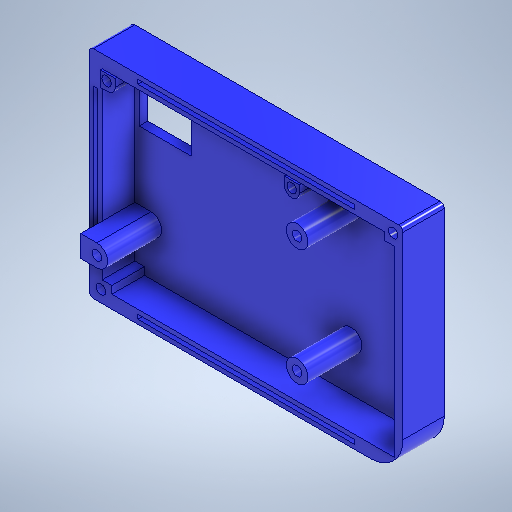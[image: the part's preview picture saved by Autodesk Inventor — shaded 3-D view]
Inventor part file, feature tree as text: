
AUTODESK INVENTOR PART (.ipt)
format: ipt  version: 2025.2 (Build 292293000, 293)  size: 788,992 bytes
history: native  units: mm
features: projected_geometry x22, sketch x19, extrude x13, fillet x2, other x1, hole x1
ambient origin geometry x8: Origin, YZ Plane, XZ Plane, XY Plane, X Axis, Y Axis, Z Axis, Center Point
bodies: Body1 (feature_tree)
feature tree (58):
  other  "Těleso1"
  extrude  "Vysunutí1"  Depth=130.0mm
  extrude  "Vysunutí2"  Depth=100.0mm
  fillet  "Zaoblení1"  Radius=30.0mm
  fillet  "Zaoblení2"  Radius=33.0mm
  extrude  "Vysunutí3"  Depth=4.0mm
  extrude  "Vysunutí4"  Depth=6.0mm
  extrude  "Vysunutí5"  Depth=6.0mm
  extrude  "Vysunutí6"  Depth=6.0mm
  extrude  "Vysunutí7"  Depth=29.0mm TaperAngle=0.0deg
  extrude  "Vysunutí8"  Depth=2.0mm
  extrude  "Vysunutí9"  Depth=2.0mm
  sketch  "Náčrt12"
  sketch  "Náčrt13"
  sketch  "Náčrt15"
  extrude  "Vysunutí10"  Depth=7.0mm
  hole  "Díra1"  [1 undecoded]
  sketch  "Náčrt19"
  extrude  "Vysunutí11"  Depth=85.0mm
  extrude  "Vysunutí13"  Depth=10.0mm
  extrude  "Vysunutí14"  Depth=8.0mm
  sketch  "Náčrt24"
  sketch  "Náčrt1"
  sketch  "Náčrt2"
  projected_geometry  "Promítnutá smyčka1"
  sketch  "Náčrt3"
  projected_geometry  "Promítnutá smyčka2"
  projected_geometry  "Promítnutá smyčka3"
  sketch  "Náčrt4"
  projected_geometry  "Promítnutá smyčka4"
  sketch  "Náčrt6"
  sketch  "Náčrt8"
  projected_geometry  "Promítnutá smyčka5"
  sketch  "Náčrt9"
  projected_geometry  "Promítnutá smyčka6"
  projected_geometry  "Promítnutá smyčka7"
  sketch  "Náčrt10"
  projected_geometry  "Promítnutá smyčka8"
  projected_geometry  "Promítnutá smyčka9"
  sketch  "Náčrt11"
  projected_geometry  "Promítnutá smyčka10"
  projected_geometry  "Promítnutá smyčka11"
  projected_geometry  "Promítnutá smyčka12"
  projected_geometry  "Promítnutá smyčka13"
  projected_geometry  "Promítnutá smyčka14"
  projected_geometry  "Promítnutá smyčka16"
  sketch  "Náčrt16"
  sketch  "Náčrt17"
  projected_geometry  "Promítnutá smyčka17"
  projected_geometry  "Promítnutá smyčka18"
  projected_geometry  "Promítnutá smyčka19"
  projected_geometry  "Promítnutá smyčka20"
  sketch  "Náčrt20"
  projected_geometry  "Promítnutá smyčka21"
  sketch  "Náčrt22"
  projected_geometry  "Promítnutá smyčka23"
  projected_geometry  "Promítnutá smyčka24"
  sketch  "Náčrt23"
note: 1 required parameter value undecoded (feature->parameter linkage not recoverable at this tier; creation-order binding heuristic only, values carry confidence <= 0.55)
